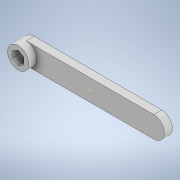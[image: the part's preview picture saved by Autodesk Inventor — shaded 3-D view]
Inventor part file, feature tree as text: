
AUTODESK INVENTOR PART (.ipt)
format: ipt  version: 2020.2 (Build 242310000, 310)  size: 125,440 bytes
history: native  units: in
note: dims shown in document units (in); Inventor stores cm internally (conversion verified against a paired STEP export)
features: sketch x4, extrude x3, fillet x1
ambient origin geometry x8: Origin, YZ Plane, XZ Plane, XY Plane, X Axis, Y Axis, Z Axis, Center Point
bodies: Solid1 (feature_tree)
feature tree (8):
  extrude  "Extrusion1"  Depth=1.0in
  fillet  "Fillet1"  Radius=0.375in
  sketch  "Sketch2"  dims[d4=0.5in d5=0.27in]
  sketch  "Sketch3"  dims[d6=0.375in d7=0.0in d8=1.0in d9=0.0in]
  extrude  "Extrusion2"  Depth=0.5in
  extrude  "Extrusion3"  Depth=1.0in TaperAngle=0.0deg
  sketch  "Sketch1"  dims[d0=7.0in d1=1.0in d2=0.375in d3=0.0in]
  sketch  "Sketch4"
